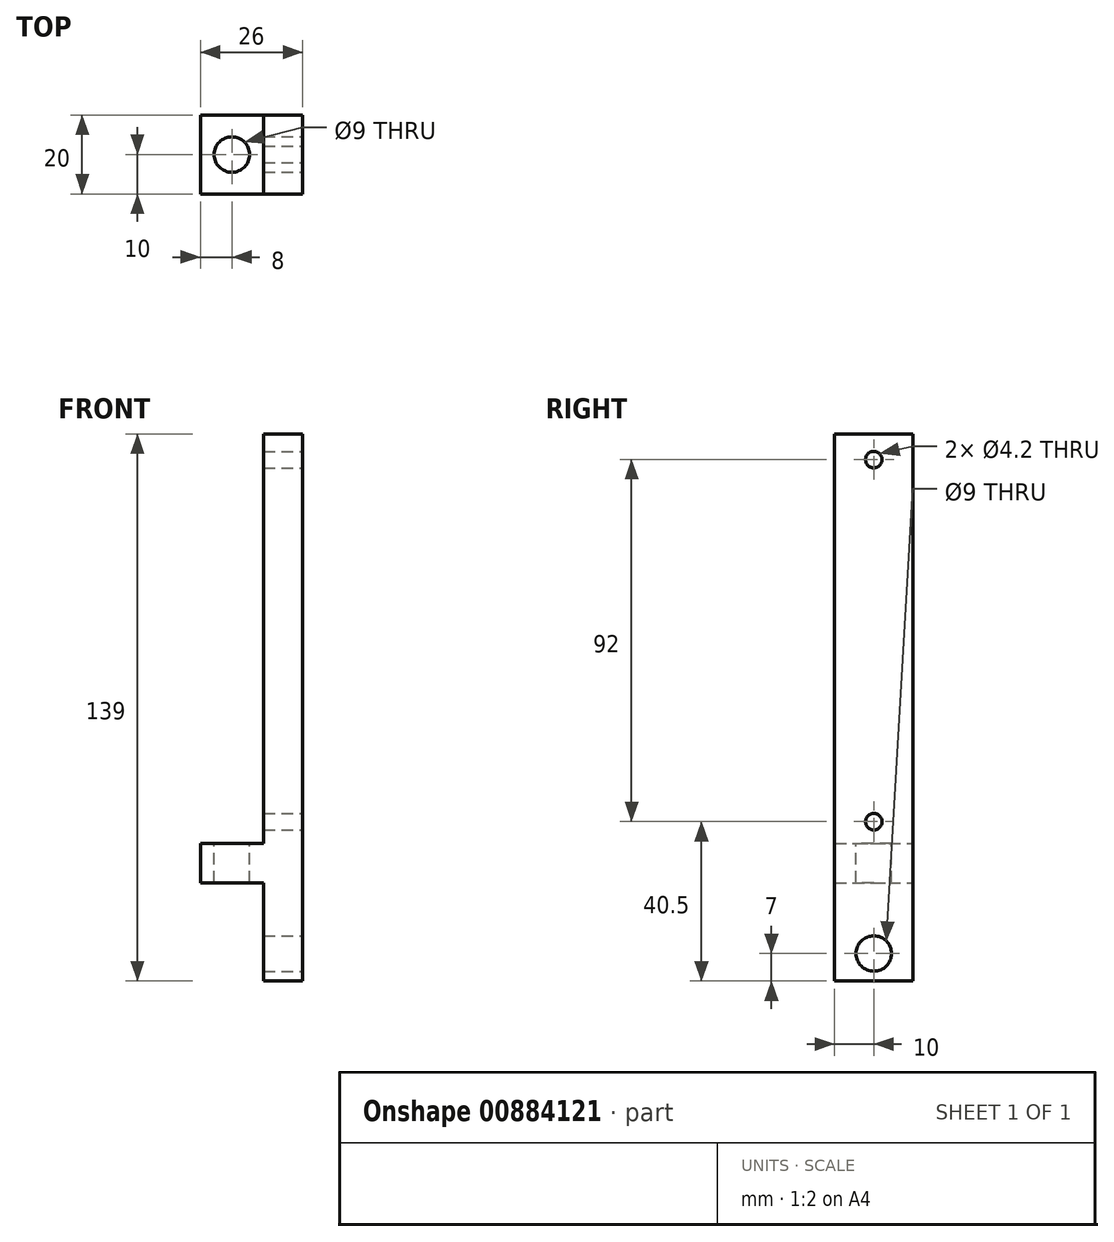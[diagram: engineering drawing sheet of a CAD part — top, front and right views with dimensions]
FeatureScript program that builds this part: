
annotation { "Feature Type Name" : "Feature", "Feature Type Description" : "" }
export const myFeature = defineFeature(function(context is Context, id is Id, definition is map)
    precondition{}
    {
        {
            var Q0;
            Q0=qCreatedBy(makeId("Front.planeOp"),FACE);
            var sketch = newSketch(context, id + "F0", { "sketchPlane" : qUnion([Q0])});
            skLineSegment(sketch, "E0", {"start": v(0, 0) * mm, "end": v(0, 104) * mm});
            skLineSegment(sketch, "E1", {"start": v(0, 104) * mm, "end": v(10, 104) * mm});
            skLineSegment(sketch, "E2", {"start": v(10, 104) * mm, "end": v(10, -35) * mm});
            skLineSegment(sketch, "E3", {"start": v(10, -35) * mm, "end": v(0, -35) * mm});
            skLineSegment(sketch, "E4", {"start": v(0, -35) * mm, "end": v(0, -10) * mm});
            skLineSegment(sketch, "E5", {"start": v(0, -10) * mm, "end": v(-16, -10) * mm});
            skLineSegment(sketch, "E6", {"start": v(-16, -10) * mm, "end": v(-16, 0) * mm});
            skLineSegment(sketch, "E7", {"start": v(-16, 0) * mm, "end": v(0, 0) * mm});
            skSolve(sketch);
        }
        {
            var Q0;
            Q0=makeQuery(id+"F0.imprint","IMPRINT",FACE,{"disambiguationData":[TD([[makeQuery(id+"F0.imprint","IMPRINT",EDGE,{"derivedFrom":sQuery(id+"F0.wireOp",EDGE,"E0")}),-1.0]])]});
            extrude(context, id + "F1", {"entities" : qUnion([Q0]), "depth" : 20 * mm, "offsetDistance" : 25 * mm});
        }
        {
            var Q0;
            Q0=makeQuery(id+"F1.opExtrude","SWEPT_FACE",FACE,{"disambiguationData":[OSD([sQuery(id+"F0.wireOp",EDGE,"E7")])]});
            var sketch = newSketch(context, id + "F2", { "sketchPlane" : qUnion([Q0])});
            skPoint(sketch, "E8", {"position": v(-8, -10) * mm});
            skPoint(sketch, "E8.positionSnap0", {"position": v(0, -10) * mm});
            skSolve(sketch);
        }
        {
            var Q0;
            Q0=sQuery(id+"F2.wireOp",VERTEX,"E8");
            var Q1;
            Q1=makeQuery(id+"F1.opExtrude","SWEPT_BODY",BODY,{"disambiguationData":[OSD([sQuery(id+"F0.wireOp",EDGE,"E0"),sQuery(id+"F0.wireOp",EDGE,"E1"),sQuery(id+"F0.wireOp",EDGE,"E2"),sQuery(id+"F0.wireOp",EDGE,"E3"),sQuery(id+"F0.wireOp",EDGE,"E4"),sQuery(id+"F0.wireOp",EDGE,"E5"),sQuery(id+"F0.wireOp",EDGE,"E6"),sQuery(id+"F0.wireOp",EDGE,"E7")])]});
            hole(context, id + "F3", {"style" : HoleStyle.SIMPLE, "endStyle" : HoleEndStyle.THROUGH, "standardTappedOrClearance" : lookupTablePath({ "fit" : "Normal", "standard" : "ISO", "size" : "M8", "type" : "Clearance" }), "standardBlindInLast" : lookupTablePath({ "fit" : "Normal", "standard" : "ISO", "size" : "M8", "type" : "Clearance" }), "holeDiameter" : 9 * mm, "majorDiameter" : 5 * mm, "isTappedThrough" : true, "tappedDepth" : 5.5 * mm, "tapClearance" : 3, "locations" : qUnion([Q0]), "scope" : qUnion([Q1])});
        }
        {
            var Q0;
            Q0=makeQuery(id+"F1.opExtrude","SWEPT_FACE",FACE,{"disambiguationData":[OSD([sQuery(id+"F0.wireOp",EDGE,"E2")])]});
            var sketch = newSketch(context, id + "F4", { "sketchPlane" : qUnion([Q0])});
            skPoint(sketch, "E9", {"position": v(-10, -28) * mm});
            skPoint(sketch, "E9.positionSnap0", {"position": v(-10, -35) * mm});
            skSolve(sketch);
        }
        {
            var Q0;
            Q0=sQuery(id+"F4.wireOp",VERTEX,"E9");
            var Q1;
            Q1=makeQuery(id+"F1.opExtrude","SWEPT_BODY",BODY,{"disambiguationData":[OSD([sQuery(id+"F0.wireOp",EDGE,"E0"),sQuery(id+"F0.wireOp",EDGE,"E1"),sQuery(id+"F0.wireOp",EDGE,"E2"),sQuery(id+"F0.wireOp",EDGE,"E3"),sQuery(id+"F0.wireOp",EDGE,"E4"),sQuery(id+"F0.wireOp",EDGE,"E5"),sQuery(id+"F0.wireOp",EDGE,"E6"),sQuery(id+"F0.wireOp",EDGE,"E7")])]});
            hole(context, id + "F5", {"style" : HoleStyle.SIMPLE, "endStyle" : HoleEndStyle.THROUGH, "standardTappedOrClearance" : lookupTablePath({ "fit" : "Normal", "standard" : "ISO", "size" : "M8", "type" : "Clearance" }), "standardBlindInLast" : lookupTablePath({ "fit" : "Normal", "standard" : "ISO", "size" : "M8", "type" : "Clearance" }), "holeDiameter" : 9 * mm, "majorDiameter" : 5 * mm, "isTappedThrough" : true, "tappedDepth" : 5.5 * mm, "tapClearance" : 3, "locations" : qUnion([Q0]), "scope" : qUnion([Q1])});
        }
        {
            var Q0;
            Q0=makeQuery(id+"F1.opExtrude","SWEPT_FACE",FACE,{"disambiguationData":[OSD([sQuery(id+"F0.wireOp",EDGE,"E2")])]});
            var sketch = newSketch(context, id + "F6", { "sketchPlane" : qUnion([Q0])});
            skPoint(sketch, "E10", {"position": v(-10, 97.5) * mm});
            skPoint(sketch, "E10.positionSnap0", {"position": v(-10, 104) * mm});
            skPoint(sketch, "E11", {"position": v(-10, 5.5) * mm});
            skSolve(sketch);
        }
        {
            var Q0;
            Q0=sQuery(id+"F6.wireOp",VERTEX,"E10");
            var Q1;
            Q1=sQuery(id+"F6.wireOp",VERTEX,"E11");
            var Q2;
            Q2=makeQuery(id+"F1.opExtrude","SWEPT_BODY",BODY,{"disambiguationData":[OSD([sQuery(id+"F0.wireOp",EDGE,"E0"),sQuery(id+"F0.wireOp",EDGE,"E1"),sQuery(id+"F0.wireOp",EDGE,"E2"),sQuery(id+"F0.wireOp",EDGE,"E3"),sQuery(id+"F0.wireOp",EDGE,"E4"),sQuery(id+"F0.wireOp",EDGE,"E5"),sQuery(id+"F0.wireOp",EDGE,"E6"),sQuery(id+"F0.wireOp",EDGE,"E7")])]});
            hole(context, id + "F7", {"style" : HoleStyle.SIMPLE, "endStyle" : HoleEndStyle.THROUGH, "standardTappedOrClearance" : lookupTablePath({ "standard" : "ISO", "engagement" : "75%", "pitch" : "0.8 mm", "size" : "M5", "type" : "Tapped" }), "standardBlindInLast" : lookupTablePath({ "standard" : "ISO", "engagement" : "75%", "pitch" : "0.8 mm", "size" : "M5", "type" : "Tapped" }), "holeDiameter" : 4.2 * mm, "majorDiameter" : 5 * mm, "showTappedDepth" : true, "isTappedThrough" : true, "tappedDepth" : 5.5 * mm, "tapClearance" : 3, "locations" : qUnion([Q0, Q1]), "scope" : qUnion([Q2])});
        }
    });
